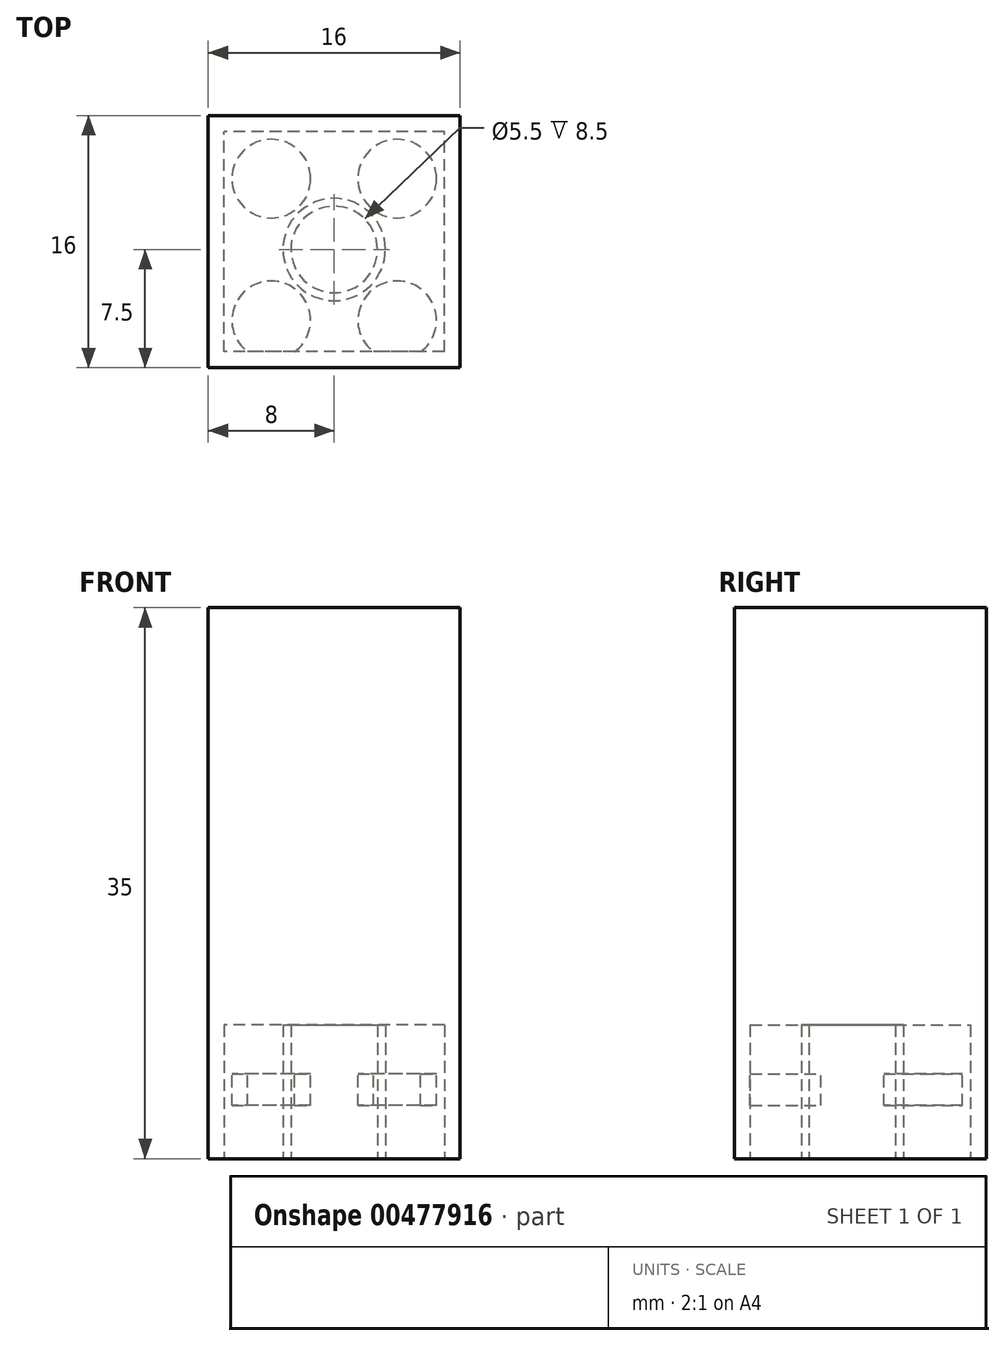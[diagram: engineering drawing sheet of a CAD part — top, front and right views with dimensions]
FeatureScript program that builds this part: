
annotation { "Feature Type Name" : "Feature", "Feature Type Description" : "" }
export const myFeature = defineFeature(function(context is Context, id is Id, definition is map)
    precondition{}
    {
        {
            var Q0;
            Q0=qCreatedBy(makeId("Right.planeOp"),FACE);
            var sketch = newSketch(context, id + "F0", { "sketchPlane" : qUnion([Q0])});
            skLineSegment(sketch, "E0.bottom", {"start": v(-7.5, 4.62) * mm, "end": v(8.5, 4.62) * mm});
            skLineSegment(sketch, "E0.top", {"start": v(-7.5, -5.38) * mm, "end": v(8.5, -5.38) * mm});
            skLineSegment(sketch, "E0.left", {"start": v(-7.5, 4.62) * mm, "end": v(-7.5, -5.38) * mm});
            skLineSegment(sketch, "E0.right", {"start": v(8.5, 4.62) * mm, "end": v(8.5, -5.38) * mm});
            skSolve(sketch);
        }
        {
            var Q0;
            Q0 = qSketchRegion(id + "F0", true);
            extrude(context, id + "F1", {"entities" : qUnion([Q0]), "depth" : 16 * mm});
        }
        {
            var Q0;
            Q0=makeQuery(id+"F1.opExtrude","SWEPT_FACE",FACE,{"disambiguationData":[OSD([sQuery(id+"F0.wireOp",EDGE,"E0.top")])]});
            var sketch = newSketch(context, id + "F2", { "sketchPlane" : qUnion([Q0])});
            skCircle(sketch, "E1", {"center": v(8, 0) * mm, "radius": 3.25 * mm});
            skPoint(sketch, "E1.centerSnap0", {"position": v(8, 7.5) * mm});
            skLineSegment(sketch, "E2.0", {"start": v(15, -7.5) * mm, "end": v(1, -7.5) * mm});
            skLineSegment(sketch, "E2.1", {"start": v(15, 6.5) * mm, "end": v(15, -7.5) * mm});
            skLineSegment(sketch, "E2.2", {"start": v(15, 6.5) * mm, "end": v(1, 6.5) * mm});
            skLineSegment(sketch, "E2.3", {"start": v(1, 6.5) * mm, "end": v(1, -7.5) * mm});
            skCircle(sketch, "E3", {"center": v(8, 0) * mm, "radius": 2.75 * mm});
            skSolve(sketch);
        }
        {
            var Q0;
            Q0=makeQuery(id+"F2.imprint","IMPRINT",FACE,{"disambiguationData":[TD([[makeQuery(id+"F2.imprint","IMPRINT",EDGE,{"derivedFrom":sQuery(id+"F2.wireOp",EDGE,"E1")}),-1.0]])]});
            var Q1;
            Q1=makeQuery(id+"F2.imprint","IMPRINT",FACE,{"disambiguationData":[TD([[makeQuery(id+"F2.imprint","IMPRINT",EDGE,{"derivedFrom":sQuery(id+"F2.wireOp",EDGE,"E3")}),1.0]])]});
            extrude(context, id + "F3", {"entities" : qUnion([Q0, Q1]), "operationType" : NewBodyOperationType.REMOVE, "oppositeDirection" : true, "depth" : 8.5 * mm});
        }
        {
            var Q0;
            Q0=qCreatedBy(makeId("Top.planeOp"),FACE);
            var sketch = newSketch(context, id + "F4", { "sketchPlane" : qUnion([Q0])});
            skCircle(sketch, "E4", {"center": v(4, 4.5) * mm, "radius": 2.5 * mm});
            skCircle(sketch, "E5.MirrorC", {"center": v(4, -4.5) * mm, "radius": 2.5 * mm});
            skLineSegment(sketch, "E6", {"start": v(0, 0) * mm, "end": v(16, 0) * mm, "construction": true});
            skLineSegment(sketch, "E7", {"start": v(8, 0) * mm, "end": v(8, 8) * mm});
            skCircle(sketch, "E8.MirrorC", {"center": v(12, 4.5) * mm, "radius": 2.5 * mm});
            skCircle(sketch, "E9.MirrorC", {"center": v(12, -4.5) * mm, "radius": 2.5 * mm});
            skSolve(sketch);
        }
        {
            var Q0;
            Q0=makeQuery(id+"F1.opExtrude","SWEPT_FACE",FACE,{"disambiguationData":[OSD([sQuery(id+"F0.wireOp",EDGE,"E0.bottom")])]});
            extrude(context, id + "F5", {"entities" : qUnion([Q0]), "operationType" : NewBodyOperationType.ADD, "depth" : 25 * mm});
        }
        {
            var Q0;
            Q0 = qSketchRegion(id + "F4", true);
            var Q1;
            Q1=makeQuery(id+"F1.opExtrude","SWEPT_FACE",FACE,{"disambiguationData":[OSD([sQuery(id+"F0.wireOp",EDGE,"E0.bottom")])]});
            extrude(context, id + "F6", {"entities" : qUnion([Q0, Q1]), "operationType" : NewBodyOperationType.ADD, "oppositeDirection" : true, "depth" : 2 * mm});
        }
    });
